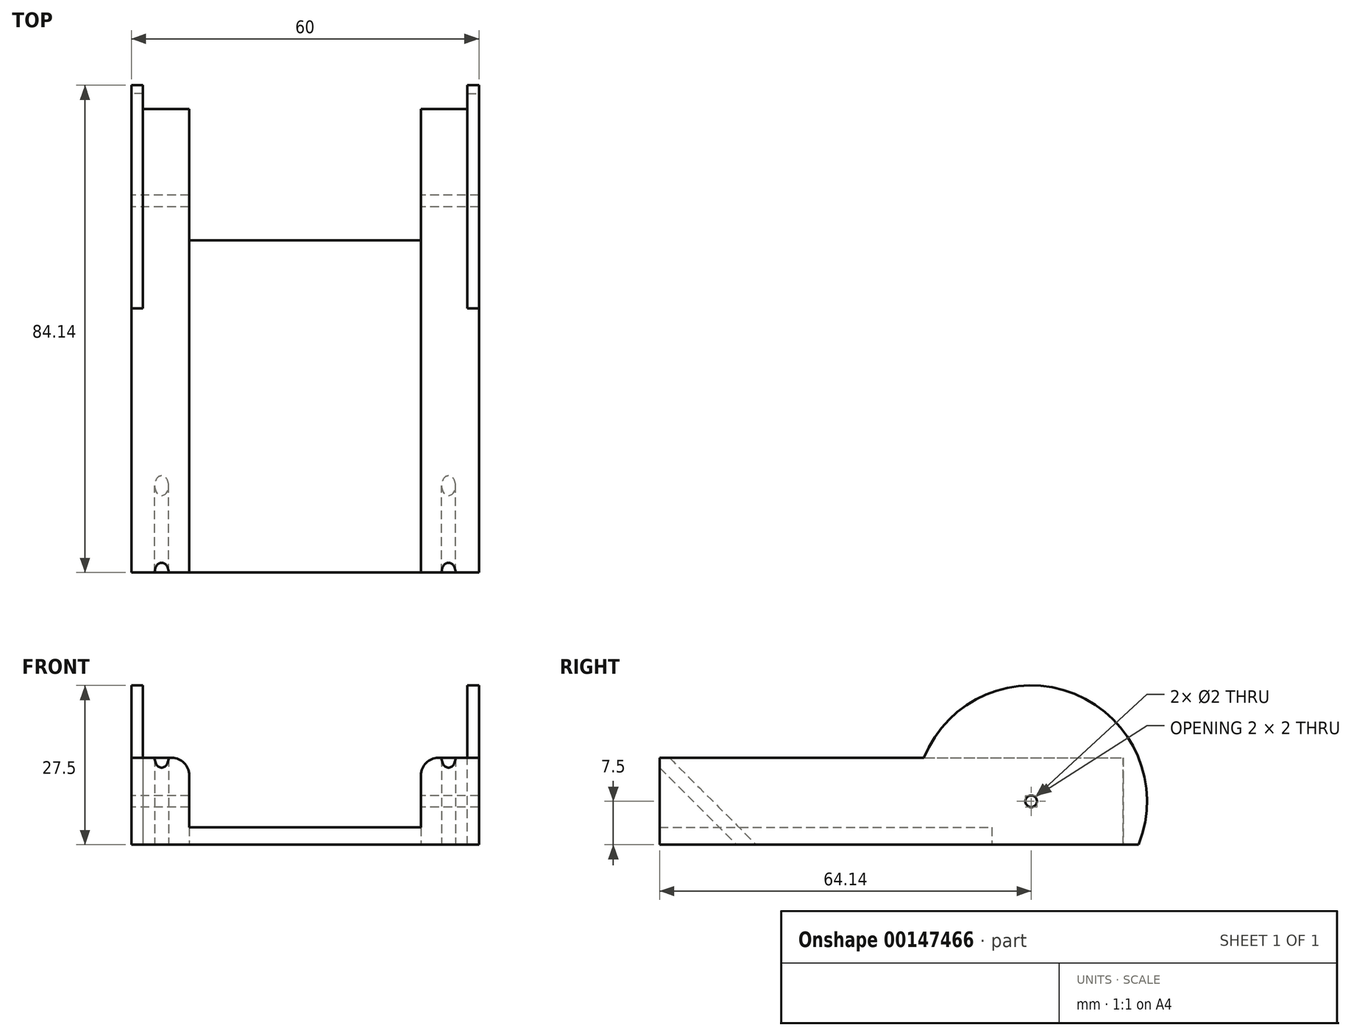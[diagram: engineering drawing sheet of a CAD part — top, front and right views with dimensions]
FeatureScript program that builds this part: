
annotation { "Feature Type Name" : "Feature", "Feature Type Description" : "" }
export const myFeature = defineFeature(function(context is Context, id is Id, definition is map)
    precondition{}
    {
        {
            var Q0;
            Q0=qCreatedBy(makeId("Top.planeOp"),FACE);
            var Q1;
            Q1=qCreatedBy(makeId("Front.planeOp"),FACE);
            cPlane(context, id + "F0", {"entities" : qUnion([Q0, Q1]), "cplaneType" : CPlaneType.MID_PLANE, "offset" : 25 * mm, "flipAlignment" : true, "width" : 150 * mm, "height" : 150 * mm});
        }
        {
            var Q0;
            Q0=qCreatedBy(id+"F0.planeOp",FACE);
            var sketch = newSketch(context, id + "F1", { "sketchPlane" : qUnion([Q0])});
            skLineSegment(sketch, "E0", {"start": v(-24.13, 0) * mm, "end": v(24.13, 0) * mm});
            skCircle(sketch, "E1", {"center": v(-24.13, 0) * mm, "radius": 1 * mm});
            skCircle(sketch, "E2", {"center": v(24.13, 0) * mm, "radius": 1 * mm});
            skLineSegment(sketch, "E3", {"start": v(0, 0) * mm, "end": v(0, -22) * mm});
            skSolve(sketch);
        }
        {
            var Q0;
            Q0=qCreatedBy(makeId("Front.planeOp"),FACE);
            var sketch = newSketch(context, id + "F2", { "sketchPlane" : qUnion([Q0])});
            skLineSegment(sketch, "E4.bottom", {"start": v(-30, 0) * mm, "end": v(30, 0) * mm});
            skLineSegment(sketch, "E4.top", {"start": v(-30, 15) * mm, "end": v(-23, 15) * mm});
            skLineSegment(sketch, "E4.left", {"start": v(-30, 0) * mm, "end": v(-30, 15) * mm});
            skLineSegment(sketch, "E4.right", {"start": v(30, 0) * mm, "end": v(30, 15) * mm});
            skPoint(sketch, "E4.middle", {"position": v(0, 7.5) * mm});
            skLineSegment(sketch, "E5.top", {"start": v(-20, 3) * mm, "end": v(20, 3) * mm});
            skLineSegment(sketch, "E5.left", {"start": v(-20, 12) * mm, "end": v(-20, 3) * mm});
            skLineSegment(sketch, "E5.right", {"start": v(20, 12) * mm, "end": v(20, 3) * mm});
            skPoint(sketch, "E5.middle", {"position": v(0, 9) * mm});
            skPoint(sketch, "E6.centerSnap0", {"position": v(0, 15) * mm});
            skLineSegment(sketch, "E7.trimOffspring", {"start": v(23, 15) * mm, "end": v(30, 15) * mm});
            skPoint(sketch, "E8.visualSharp", {"position": v(-20, 15) * mm});
            skArc(sketch, "E8.filletArc", {"start": v(-20, 12) * mm, "mid": v(-20.88, 14.12) * mm, "end": v(-23, 15) * mm});
            skPoint(sketch, "E9.visualSharp", {"position": v(20, 15) * mm});
            skArc(sketch, "E9.filletArc", {"start": v(23, 15) * mm, "mid": v(20.88, 14.12) * mm, "end": v(20, 12) * mm});
            skCircle(sketch, "E10", {"center": v(0, 28.66) * mm, "radius": 25.4 * mm, "construction": true});
            skSolve(sketch);
        }
        {
            var Q0;
            Q0=makeQuery(id+"F2.imprint","IMPRINT",FACE,{"disambiguationData":[TD([[makeQuery(id+"F2.imprint","IMPRINT",EDGE,{"derivedFrom":sQuery(id+"F2.wireOp",EDGE,"E4.bottom")}),1.0]])]});
            extrude(context, id + "F3", {"entities" : qUnion([Q0]), "depth" : 15 * mm, "hasSecondDirection" : true, "secondDirectionOppositeDirection" : true, "secondDirectionDepth" : 65 * mm});
        }
        {
            var Q0;
            Q0=qCreatedBy(id+"F0.planeOp",FACE);
            var sketch = newSketch(context, id + "F4", { "sketchPlane" : qUnion([Q0])});
            skLineSegment(sketch, "E11", {"start": v(-24.77, 0) * mm, "end": v(24.77, 0) * mm});
            skCircle(sketch, "E12", {"center": v(-24.77, 0) * mm, "radius": 1.2 * mm});
            skCircle(sketch, "E13", {"center": v(24.77, 0) * mm, "radius": 1.2 * mm});
            skSolve(sketch);
        }
        {
            var Q0;
            Q0=qSketchRegion(id+"F4",true);
            extrude(context, id + "F5", {"entities" : qUnion([Q0]), "operationType" : NewBodyOperationType.REMOVE, "depth" : 124.25 * mm, "hasSecondDirection" : true, "secondDirectionOppositeDirection" : true, "secondDirectionDepth" : 109.5 * mm});
        }
        {
            var Q0;
            Q0=makeQuery(id+"F3.opExtrude","SWEPT_FACE",FACE,{"disambiguationData":[OSD([sQuery(id+"F2.wireOp",EDGE,"E4.right")])]});
            var sketch = newSketch(context, id + "F6", { "sketchPlane" : qUnion([Q0])});
            skLineSegment(sketch, "E14", {"start": v(-15, 7.5) * mm, "end": v(49.14, 7.5) * mm, "construction": true});
            skCircle(sketch, "E15", {"center": v(49.14, 7.5) * mm, "radius": 20 * mm});
            skSolve(sketch);
        }
        {
            var Q0;
            Q0=makeQuery(id+"F3.opExtrude","SWEPT_FACE",FACE,{"disambiguationData":[OSD([sQuery(id+"F2.wireOp",EDGE,"E4.left")])]});
            var sketch = newSketch(context, id + "F7", { "sketchPlane" : qUnion([Q0])});
            skLineSegment(sketch, "E16", {"start": v(15, 7.5) * mm, "end": v(-49.14, 7.5) * mm, "construction": true});
            skCircle(sketch, "E17", {"center": v(-49.14, 7.5) * mm, "radius": 20 * mm});
            skSolve(sketch);
        }
        {
            var Q0;
            Q0 = qSketchRegion(id + "F6", true);
            extrude(context, id + "F8", {"entities" : qUnion([Q0]), "operationType" : NewBodyOperationType.ADD, "oppositeDirection" : true, "depth" : 2 * mm});
        }
        {
            var Q0;
            Q0 = qSketchRegion(id + "F7", true);
            extrude(context, id + "F9", {"entities" : qUnion([Q0]), "operationType" : NewBodyOperationType.ADD, "oppositeDirection" : true, "depth" : 2 * mm});
        }
        {
            var Q0;
            Q0=qCreatedBy(makeId("Right.planeOp"),FACE);
            var sketch = newSketch(context, id + "F10", { "sketchPlane" : qUnion([Q0])});
            skLineSegment(sketch, "E18.bottom", {"start": v(0, 0) * mm, "end": v(125.27, 0) * mm});
            skLineSegment(sketch, "E18.top", {"start": v(0, -20.9) * mm, "end": v(125.27, -20.9) * mm});
            skLineSegment(sketch, "E18.left", {"start": v(0, 0) * mm, "end": v(0, -20.9) * mm});
            skLineSegment(sketch, "E18.right", {"start": v(125.27, 0) * mm, "end": v(125.27, -20.9) * mm});
            skSolve(sketch);
        }
        {
            var Q0;
            Q0=qSketchRegion(id+"F10",true);
            extrude(context, id + "F11", {"entities" : qUnion([Q0]), "operationType" : NewBodyOperationType.REMOVE, "endBound" : BoundingType.SYMMETRIC, "oppositeDirection" : true, "depth" : 80 * mm});
        }
        {
            var Q0;
            Q0=qCreatedBy(makeId("Top.planeOp"),FACE);
            var sketch = newSketch(context, id + "F12", { "sketchPlane" : qUnion([Q0])});
            skLineSegment(sketch, "E19.0", {"start": v(-20, 65) * mm, "end": v(20, 65) * mm});
            skLineSegment(sketch, "E20.top", {"start": v(-20, 42.37) * mm, "end": v(20, 42.37) * mm});
            skLineSegment(sketch, "E20.left", {"start": v(-20, 65) * mm, "end": v(-20, 42.37) * mm});
            skLineSegment(sketch, "E20.right", {"start": v(20, 65) * mm, "end": v(20, 42.37) * mm});
            skLineSegment(sketch, "E21.0", {"start": v(-28, 30.6) * mm, "end": v(-28, 69.14) * mm});
            skLineSegment(sketch, "E22", {"start": v(-28, 49.87) * mm, "end": v(-20, 49.87) * mm, "construction": true});
            skSolve(sketch);
        }
        {
            var Q0;
            Q0 = qSketchRegion(id + "F12", true);
            extrude(context, id + "F13", {"entities" : qUnion([Q0]), "operationType" : NewBodyOperationType.REMOVE, "depth" : 10 * mm});
        }
        {
            var Q0;
            Q0=qCreatedBy(makeId("Right.planeOp"),FACE);
            var sketch = newSketch(context, id + "F14", { "sketchPlane" : qUnion([Q0])});
            skArc(sketch, "E23.0", {"start": v(30.6, 15) * mm, "mid": v(56.64, 26.04) * mm, "end": v(67.68, 0) * mm});
            skCircle(sketch, "E24", {"center": v(49.14, 7.5) * mm, "radius": 1 * mm});
            skSolve(sketch);
        }
        {
            var Q0;
            Q0 = qSketchRegion(id + "F14", true);
            extrude(context, id + "F15", {"entities" : qUnion([Q0]), "operationType" : NewBodyOperationType.REMOVE, "endBound" : BoundingType.SYMMETRIC, "depth" : 100 * mm});
        }
    });
